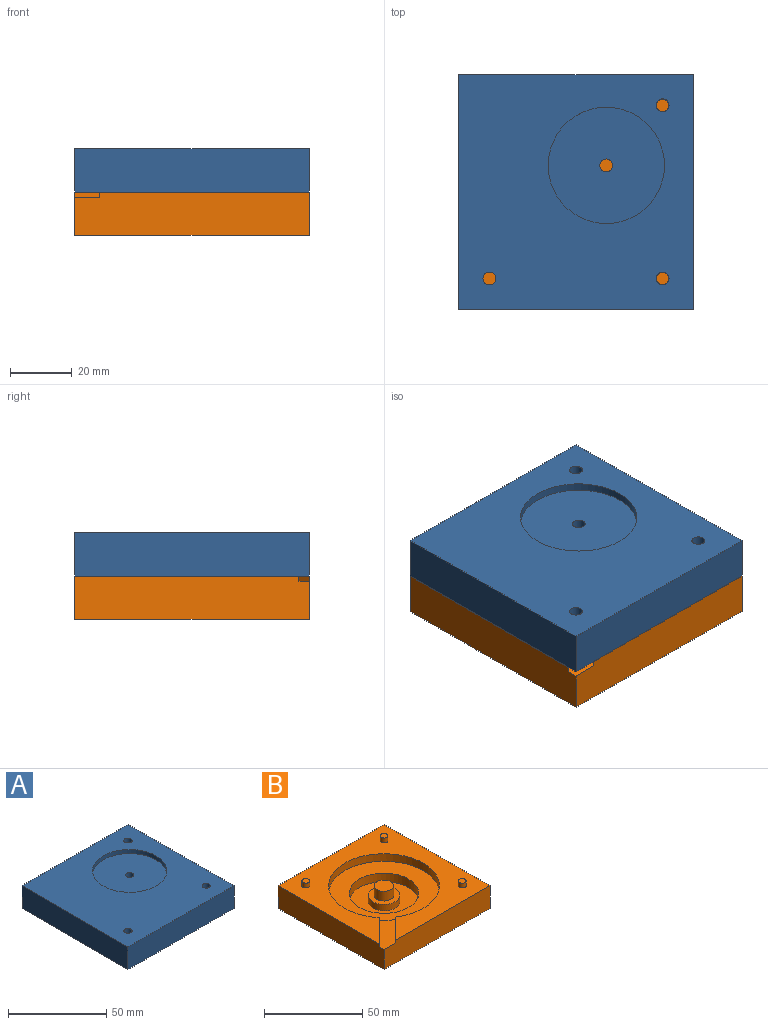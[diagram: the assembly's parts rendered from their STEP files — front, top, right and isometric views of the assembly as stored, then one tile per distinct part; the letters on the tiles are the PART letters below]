
ASSEMBLY  parts=2 mates=1
PART A: 18 faces, bbox 76.2x76.2x14.1 mm
  f0: plane 76.2x14.05mm, normal (0,1,0), area 1070.6mm2, adj f1,f3,f5,f12
  f1: plane 76.2x14.05mm, normal (-1,0,0), area 1070.6mm2, adj f0,f2,f5,f12
  f2: plane 76.2x14.05mm, normal (0,-1,0), area 1070.6mm2, adj f1,f3,f5,f12
  f3: plane 76.2x14.05mm, normal (1,0,0), area 1070.6mm2, adj f0,f2,f5,f12
  f4: cylinder r=2.1mm len=5.5mm, axis (0,0,1), area 72.6mm2, adj f9,f14
  f5: plane 76.2x76.2mm, normal (0,0,-1), area 3258.8mm2, adj f0,f1,f2,f3,f7,f8,f15,f16
  f6: plane 4x4mm, normal (0,0,-1), area 12.6mm2, adj f7
  f7: cylinder r=2mm len=4mm, axis (0,0,-1), area 37.7mm2, adj f5,f6
  f8: cylinder r=28.17mm len=56.35mm, axis (0,0,-1), area 1062.1mm2, adj f5,f9
  f9: plane 56.35x56.35mm, normal (0,0,-1), area 2401.1mm2, adj f4,f8,f10
  f10: cylinder r=5mm len=10mm, axis (0,0,1), area 188.5mm2, adj f9,f11
  f11: plane 10x10mm, normal (0,0,-1), area 78.5mm2, adj f10
  f12: plane 76.2x76.2mm, normal (0,0,1), area 4645.6mm2, adj f0,f1,f2,f3,f13,f15,f16,f17
  f13: cylinder r=18.88mm len=37.75mm, axis (0,0,1), area 302.4mm2, adj f12,f14
  f14: plane 37.75x37.75mm, normal (0,0,1), area 1105.4mm2, adj f4,f13
  f15: cylinder r=2.1mm len=14.05mm, axis (0,0,-1), area 185.4mm2, adj f5,f12
  f16: cylinder r=2.1mm len=14.05mm, axis (0,0,-1), area 185.4mm2, adj f5,f12
  f17: cylinder r=2.1mm len=14.05mm, axis (0,0,-1), area 185.4mm2, adj f5,f12
PART B: 25 faces, bbox 76.2x76.2x17.1 mm
  f0: plane 35.31x35.31mm, normal (0,0,1), area 778.1mm2, adj f1,f6
  f1: cylinder r=8mm len=16mm, axis (0,0,-1), area 201.1mm2, adj f0,f2
  f2: plane 16x16mm, normal (0,0,1), area 122.5mm2, adj f1,f3
  f3: cylinder r=5mm len=10mm, axis (0,0,-1), area 188.5mm2, adj f2,f4
  f4: plane 10x10mm, normal (0,0,1), area 78.5mm2, adj f3
  f5: plane 56.35x56.35mm, normal (0,0,1), area 1514.4mm2, adj f6,f22
  f6: cylinder r=17.65mm len=35.31mm, axis (0,0,-1), area 587.9mm2, adj f0,f5
  f7: plane 4x4mm, normal (0,0,1), area 12.6mm2, adj f11
  f8: plane 4x4mm, normal (0,0,1), area 12.6mm2, adj f12
  f9: plane 4x4mm, normal (0,0,1), area 12.6mm2, adj f13
  f10: plane 76.2x76.2mm, normal (0,0,-1), area 5656.9mm2, adj f14,f15,f16,f17,f23
  f11: cylinder r=2mm len=4mm, axis (0,0,-1), area 37.7mm2, adj f7,f21
  f12: cylinder r=2mm len=4mm, axis (0,0,-1), area 37.7mm2, adj f8,f21
  f13: cylinder r=2mm len=4mm, axis (0,0,-1), area 37.7mm2, adj f9,f21
  f14: plane 76.2x14.05mm, normal (-1,0,0), area 1065mm2, adj f10,f15,f17,f19,f20,f21
  f15: plane 76.2x14.05mm, normal (0,1,0), area 1070.6mm2, adj f10,f14,f16,f21
  f16: plane 76.2x14.05mm, normal (1,0,0), area 1070.6mm2, adj f10,f15,f17,f21
  f17: plane 76.2x14.05mm, normal (0,-1,0), area 1057.1mm2, adj f10,f14,f16,f18,f19,f21
  f18: plane 14.5x14.5mm, normal (-0.71,0.71,0), area 33.8mm2, adj f17,f19,f21,f22
  f19: plane 22.72x19.94mm, normal (0,0,1), area 192.3mm2, adj f14,f17,f18,f20,f22
  f20: plane 16.56x16.56mm, normal (0.71,-0.71,0), area 38.6mm2, adj f14,f19,f21,f22
  f21: plane 76.2x76.2mm, normal (0,0,1), area 3082.9mm2, adj f11,f12,f13,f14,f15,f16,f17,f18
  f22: cylinder r=28.17mm len=56.35mm, axis (0,0,1), area 818.4mm2, adj f5,f18,f19,f20,f21
  f23: cylinder r=6.9mm len=13.8mm, axis (0,0,-1), area 86.7mm2, adj f10,f24
  f24: plane 13.8x13.8mm, normal (0,0,-1), area 149.6mm2, adj f23
PLACE A t=(8.64,37.39,-83.76)mm
PLACE B t=(8.64,37.39,-33.76)mm
MATE revolute A.f15 <-> B.f13  axis (0,0,-1) through (74.84,-28.81,-17.71)mm
